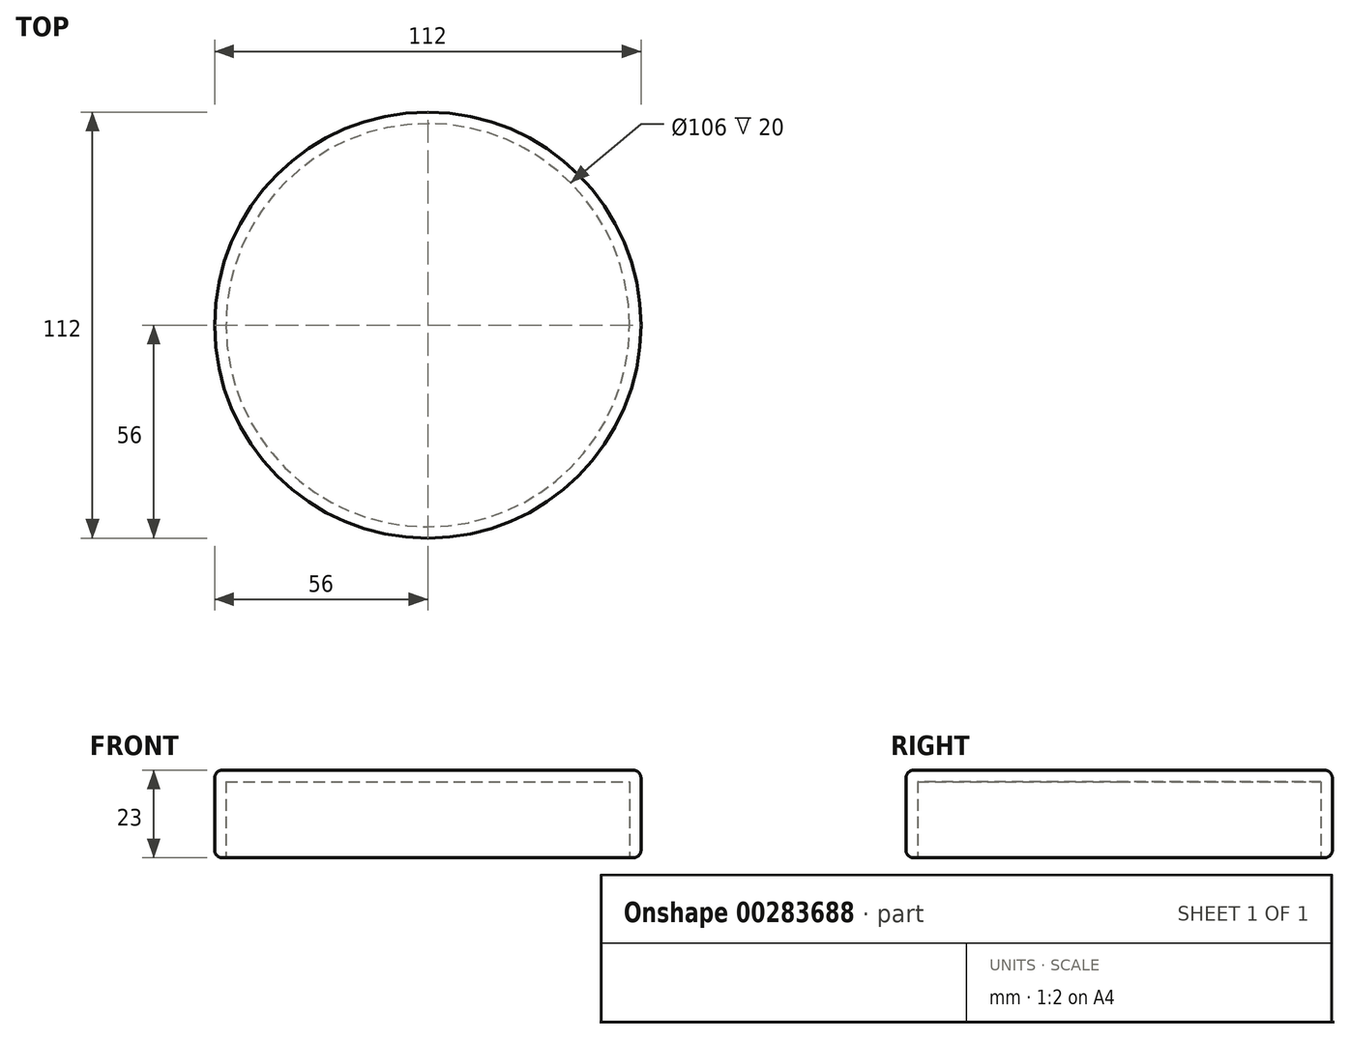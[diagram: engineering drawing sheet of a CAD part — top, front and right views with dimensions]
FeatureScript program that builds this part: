
annotation { "Feature Type Name" : "Feature", "Feature Type Description" : "" }
export const myFeature = defineFeature(function(context is Context, id is Id, definition is map)
    precondition{}
    {
        {
            var Q0;
            Q0=qCreatedBy(makeId("Front.planeOp"),FACE);
            var sketch = newSketch(context, id + "F0", { "sketchPlane" : qUnion([Q0])});
            skLineSegment(sketch, "E0", {"start": v(-53, -20) * mm, "end": v(-53, 0) * mm});
            skLineSegment(sketch, "E1", {"start": v(-53, 0) * mm, "end": v(0, 0) * mm});
            skLineSegment(sketch, "E2.0", {"start": v(-54, 3) * mm, "end": v(0, 3) * mm});
            skLineSegment(sketch, "E2.1", {"start": v(-56, -18) * mm, "end": v(-56, 1) * mm});
            skLineSegment(sketch, "E3", {"start": v(-54, -20) * mm, "end": v(-53, -20) * mm});
            skLineSegment(sketch, "E4", {"start": v(0, 0) * mm, "end": v(0, 3) * mm});
            skPoint(sketch, "E5.visualSharp", {"position": v(-56, 3) * mm});
            skArc(sketch, "E5.filletArc", {"start": v(-54, 3) * mm, "mid": v(-55.41, 2.41) * mm, "end": v(-56, 1) * mm});
            skPoint(sketch, "E6.visualSharp", {"position": v(-56, -20) * mm});
            skArc(sketch, "E6.filletArc", {"start": v(-56, -18) * mm, "mid": v(-55.41, -19.41) * mm, "end": v(-54, -20) * mm});
            skSolve(sketch);
        }
        {
            var Q0;
            Q0=makeQuery(id+"F0.imprint","IMPRINT",FACE,{"disambiguationData":[TD([[makeQuery(id+"F0.imprint","IMPRINT",EDGE,{"derivedFrom":sQuery(id+"F0.wireOp",EDGE,"E0")}),1.0]])]});
            var Q1;
            Q1=sQuery(id+"F0.wireOp",EDGE,"E4");
            revolve(context, id + "F1", {"entities" : qUnion([Q0]), "axis" : qUnion([Q1]), "revolveType" : RevolveType.FULL});
        }
    });
